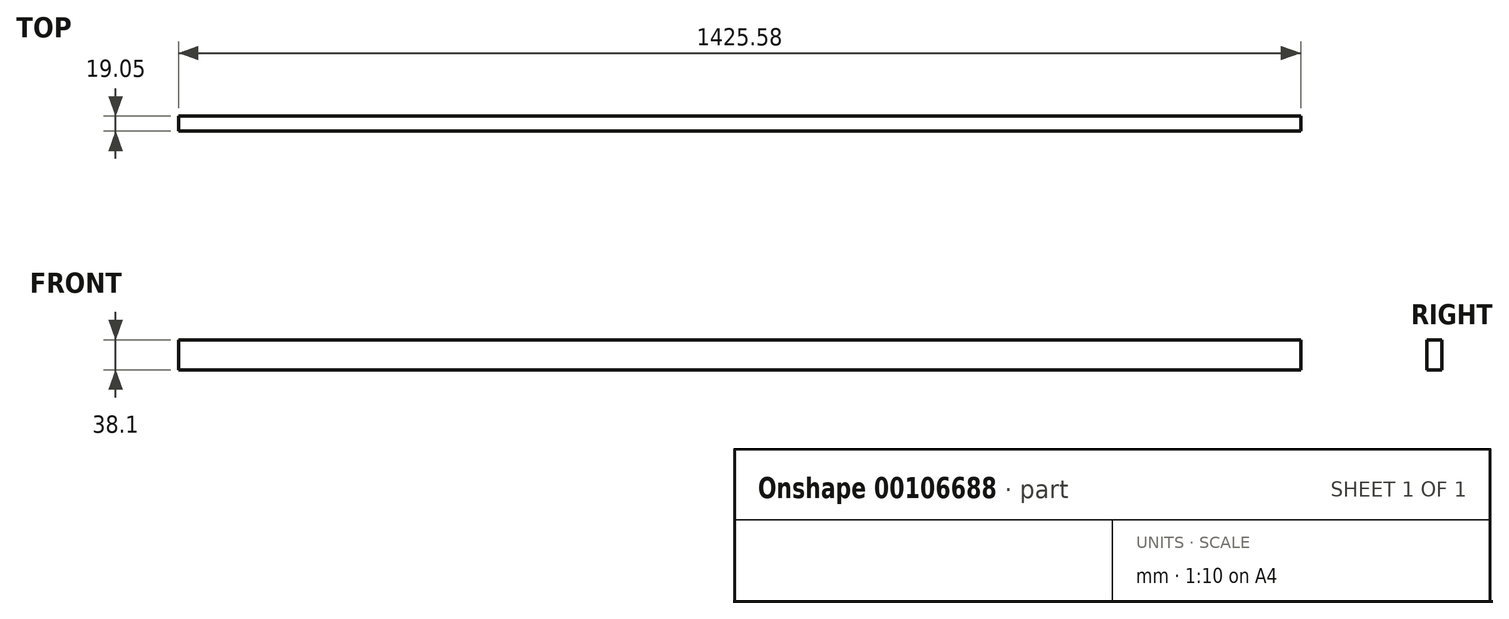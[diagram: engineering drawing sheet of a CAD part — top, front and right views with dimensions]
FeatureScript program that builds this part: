
annotation { "Feature Type Name" : "Feature", "Feature Type Description" : "" }
export const myFeature = defineFeature(function(context is Context, id is Id, definition is map)
    precondition{}
    {
        {
            var Q0;
            Q0=qCreatedBy(makeId("Front.planeOp"),FACE);
            var sketch = newSketch(context, id + "F0", { "sketchPlane" : qUnion([Q0])});
            skLineSegment(sketch, "E0.bottom", {"start": v(0, 0) * mm, "end": v(1425.58, 0) * mm});
            skLineSegment(sketch, "E0.top", {"start": v(0, 38.1) * mm, "end": v(1425.58, 38.1) * mm});
            skLineSegment(sketch, "E0.left", {"start": v(0, 0) * mm, "end": v(0, 38.1) * mm});
            skLineSegment(sketch, "E0.right", {"start": v(1425.58, 0) * mm, "end": v(1425.58, 38.1) * mm});
            skSolve(sketch);
        }
        {
            var Q0;
            Q0=makeQuery(id+"F0.imprint","IMPRINT",FACE,{"disambiguationData":[TD([[makeQuery(id+"F0.imprint","IMPRINT",EDGE,{"derivedFrom":sQuery(id+"F0.wireOp",EDGE,"E0.bottom")}),1.0]])]});
            extrude(context, id + "F1", {"entities" : qUnion([Q0]), "depth" : 19.05 * mm});
        }
    });
